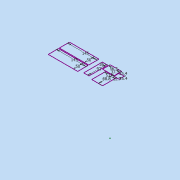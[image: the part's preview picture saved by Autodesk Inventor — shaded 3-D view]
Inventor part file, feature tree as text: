
AUTODESK INVENTOR PART (.ipt)
format: ipt  version: 2017 (Build 210142000, 142)  size: 79,872 bytes
history: native  units: in
note: dims shown in document units (in); Inventor stores cm internally (conversion verified against a paired STEP export)
features: sketch x1
ambient origin geometry x8: Origin, YZ Plane, XZ Plane, XY Plane, X Axis, Y Axis, Z Axis, Center Point
feature tree (1):
  sketch  "Sketch1"  dims[d0=2.2244in d1=1.4764in d2=2.1024in d3=2.7087in d4=3.622in d5=1.0236in d6=5.7087in d7=1.9685in d8=5.7087in d9=1.9685in d10=1.0in d11=0.5in d12=1.0in]
